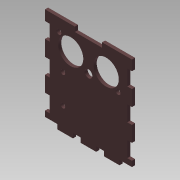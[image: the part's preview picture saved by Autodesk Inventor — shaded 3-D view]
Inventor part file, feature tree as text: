
AUTODESK INVENTOR PART (.ipt)
format: ipt  version: 2015 SP1 (Build 190203100, 203)  size: 151,552 bytes
history: native  units: mm
features: extrude x1, sketch x1
ambient origin geometry x8: Origin, YZ Plane, XZ Plane, XY Plane, X Axis, Y Axis, Z Axis, Center Point
bodies: Solid1 (feature_tree)
feature tree (2):
  extrude  "Extrusion1"  Depth=2.0mm TaperAngle=0.0deg
  sketch  "Sketch1"  dims[d1=20.0mm d3=20.0mm d4=3.0mm d5=15.0mm d6=15.0mm d7=5.0mm d8=10.0mm d9=3.0mm d10=3.0mm d12=2.0mm d13=0.0mm]
